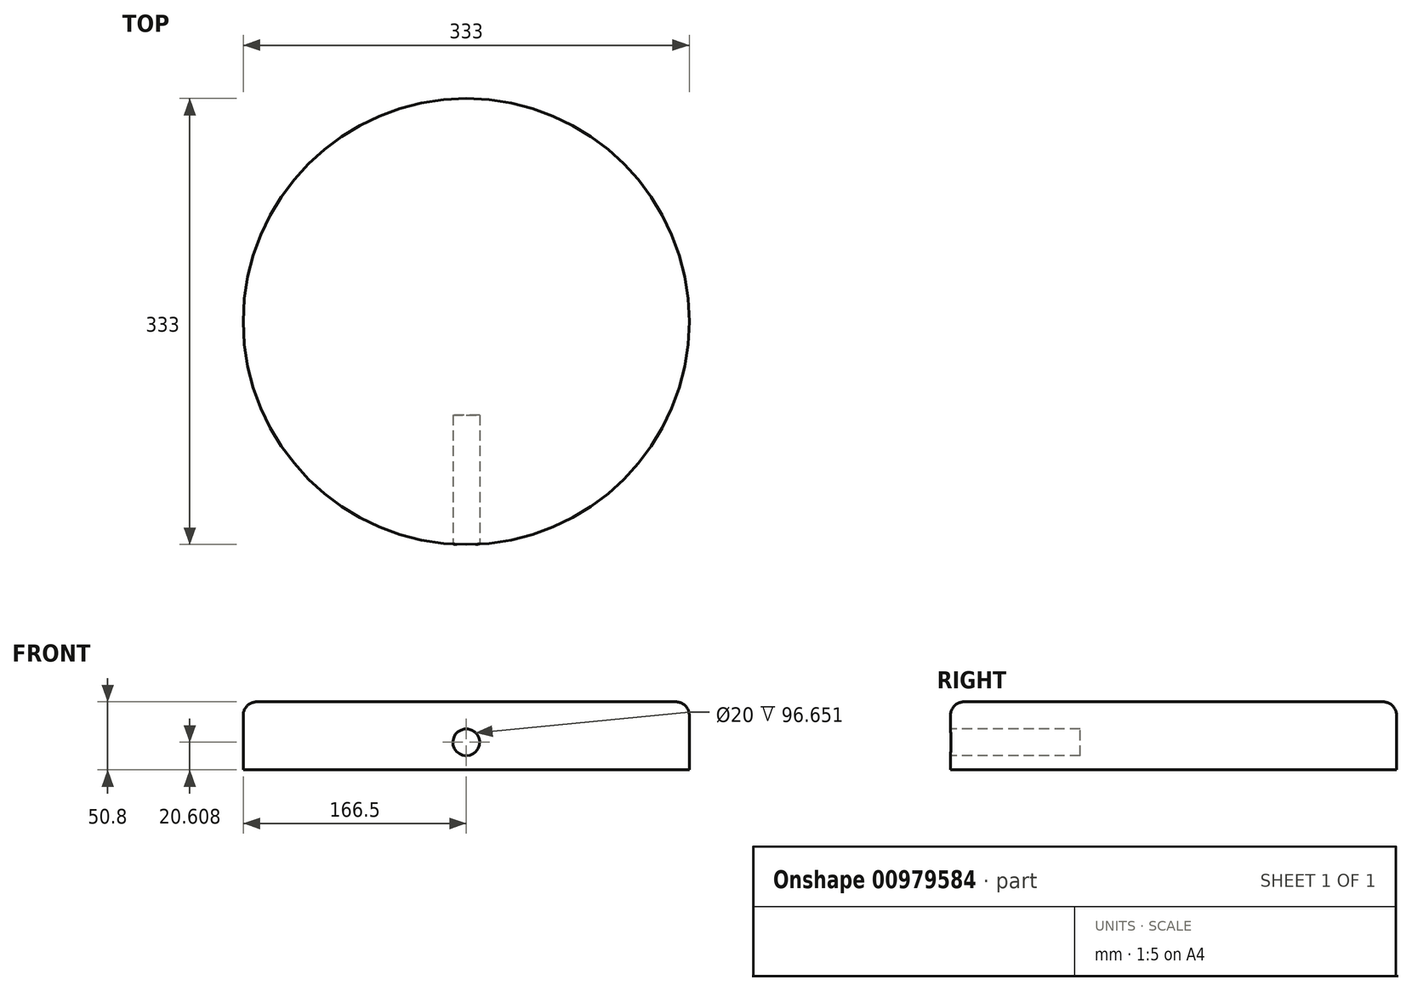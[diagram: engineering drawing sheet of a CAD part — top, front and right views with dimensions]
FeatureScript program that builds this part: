
annotation { "Feature Type Name" : "Feature", "Feature Type Description" : "" }
export const myFeature = defineFeature(function(context is Context, id is Id, definition is map)
    precondition{}
    {
        {
            var Q0;
            Q0=qCreatedBy(makeId("Top.planeOp"),FACE);
            var sketch = newSketch(context, id + "F0", { "sketchPlane" : qUnion([Q0])});
            skCircle(sketch, "E0", {"center": v(0, 0) * mm, "radius": 166.5 * mm});
            skSolve(sketch);
        }
        {
            var Q0;
            Q0 = qSketchRegion(id + "F0", true);
            extrude(context, id + "F1", {"entities" : qUnion([Q0]), "depth" : 50.8 * mm, "offsetDistance" : 25.4 * mm});
        }
        {
            var Q0;
            Q0=makeQuery(id+"F1.opExtrude","CAP_EDGE",EDGE,{"disambiguationData":[OSD([sQuery(id+"F0.wireOp",EDGE,"E0")])],"isStart":false});
            fillet(context, id + "F2", {"entities" : qUnion([Q0]), "radius" : 10 * mm, "tangentPropagation" : true, "allowEdgeOverflow" : false});
        }
        {
            var Q0;
            Q0=qCreatedBy(makeId("Front.planeOp"),FACE);
            cPlane(context, id + "F3", {"entities" : qUnion([Q0]), "cplaneType" : CPlaneType.OFFSET, "offset" : 167.13 * mm, "width" : 152.4 * mm, "height" : 152.4 * mm});
        }
        {
            var Q0;
            Q0=qCreatedBy(id+"F3.planeOp",FACE);
            var sketch = newSketch(context, id + "F4", { "sketchPlane" : qUnion([Q0])});
            skCircle(sketch, "E1", {"center": v(0, 20.6) * mm, "radius": 10 * mm});
            skSolve(sketch);
        }
        {
            var Q0;
            Q0 = qSketchRegion(id + "F4", true);
            extrude(context, id + "F5", {"entities" : qUnion([Q0]), "operationType" : NewBodyOperationType.REMOVE, "oppositeDirection" : true, "depth" : 97.28 * mm, "offsetDistance" : 25.4 * mm});
        }
    });
